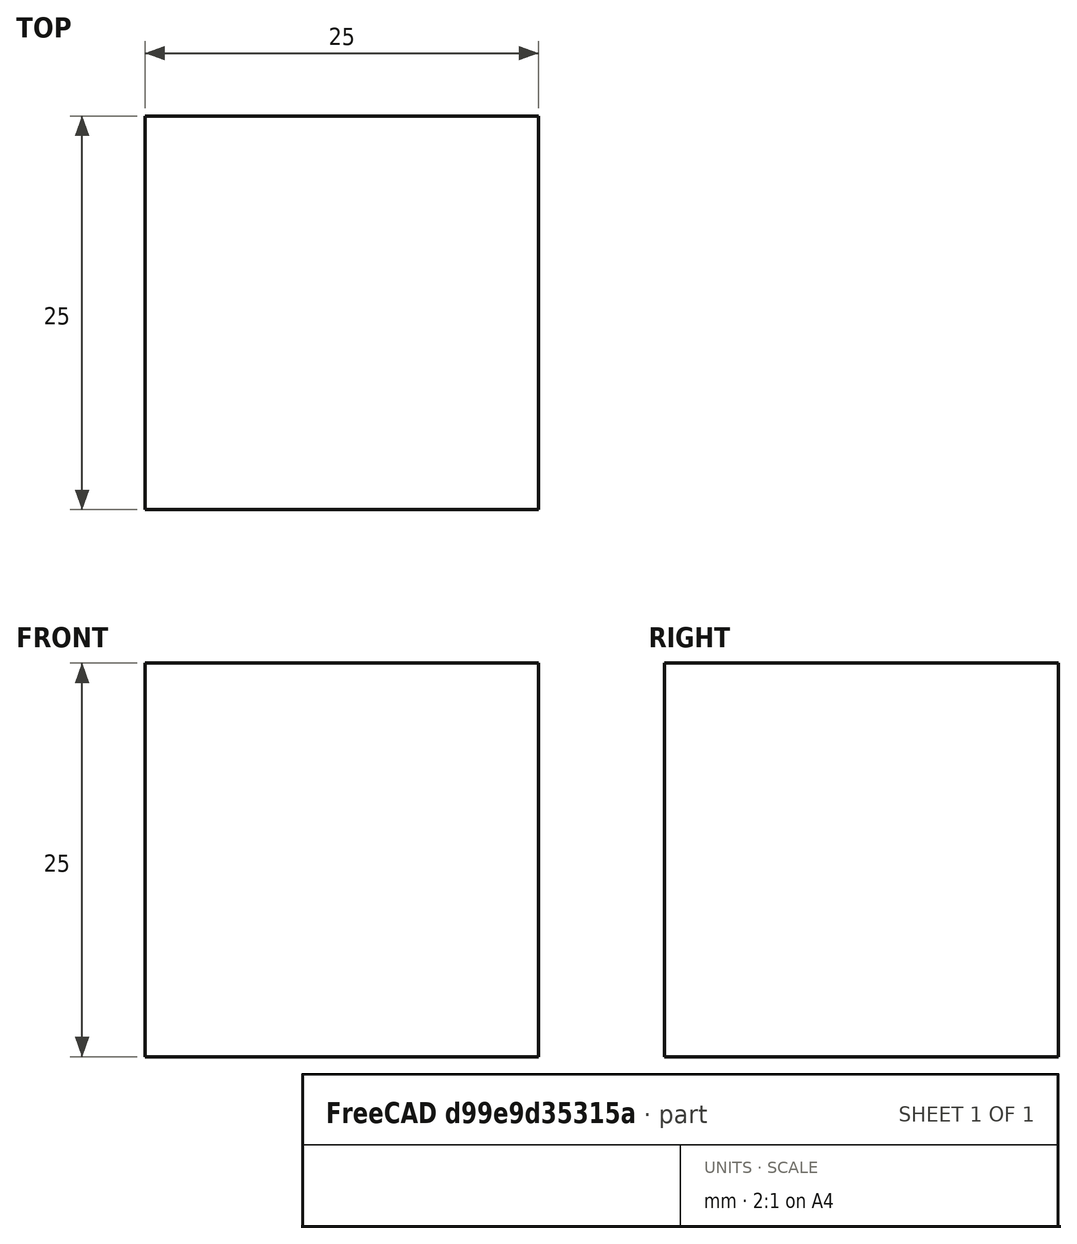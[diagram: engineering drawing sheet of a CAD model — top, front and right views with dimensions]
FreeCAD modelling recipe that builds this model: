
FCSTD DOCUMENT  (FreeCAD 0.16R)
Label: Cube
License: All rights reserved
LicenseURL: http://en.wikipedia.org/wiki/All_rights_reserved
objects: Sketcher::SketchObject×1, PartDesign::Pad×1
note: 3 computed .brp shape members not serialized (recipe doc carries the construction recipe); baked Part::Feature solids carry a one-line shape summary decoded from their .brp

FEATURE [Sketcher::SketchObject] Sketch
  sketch-geometry (4):
    g0: LineSegment StartX=0 StartY=25 StartZ=0 EndX=-25 EndY=25 EndZ=0
    g1: LineSegment StartX=-25 StartY=25 StartZ=0 EndX=-25 EndY=0 EndZ=0
    g2: LineSegment StartX=-25 StartY=0 StartZ=0 EndX=0 EndY=0 EndZ=0
    g3: LineSegment StartX=0 StartY=0 StartZ=0 EndX=0 EndY=25 EndZ=0
  constraints (11):
    c: Horizontal(g0)
    c: Coincident(g0,g1)
    c: Vertical(g1)
    c: Coincident(g1,g2)
    c: Horizontal(g2)
    c: Coincident(g2,g3)
    c: Vertical(g3)
    c: Coincident(g3,g0)
    c: Distance(g1) = 25
    c: Distance(g0) = 25
    c: Coincident(g2,g-1)
FEATURE [PartDesign::Pad] Pad
  Length = 25
  Length2 = 100
  Sketch = -> Sketch
  Type = 0
